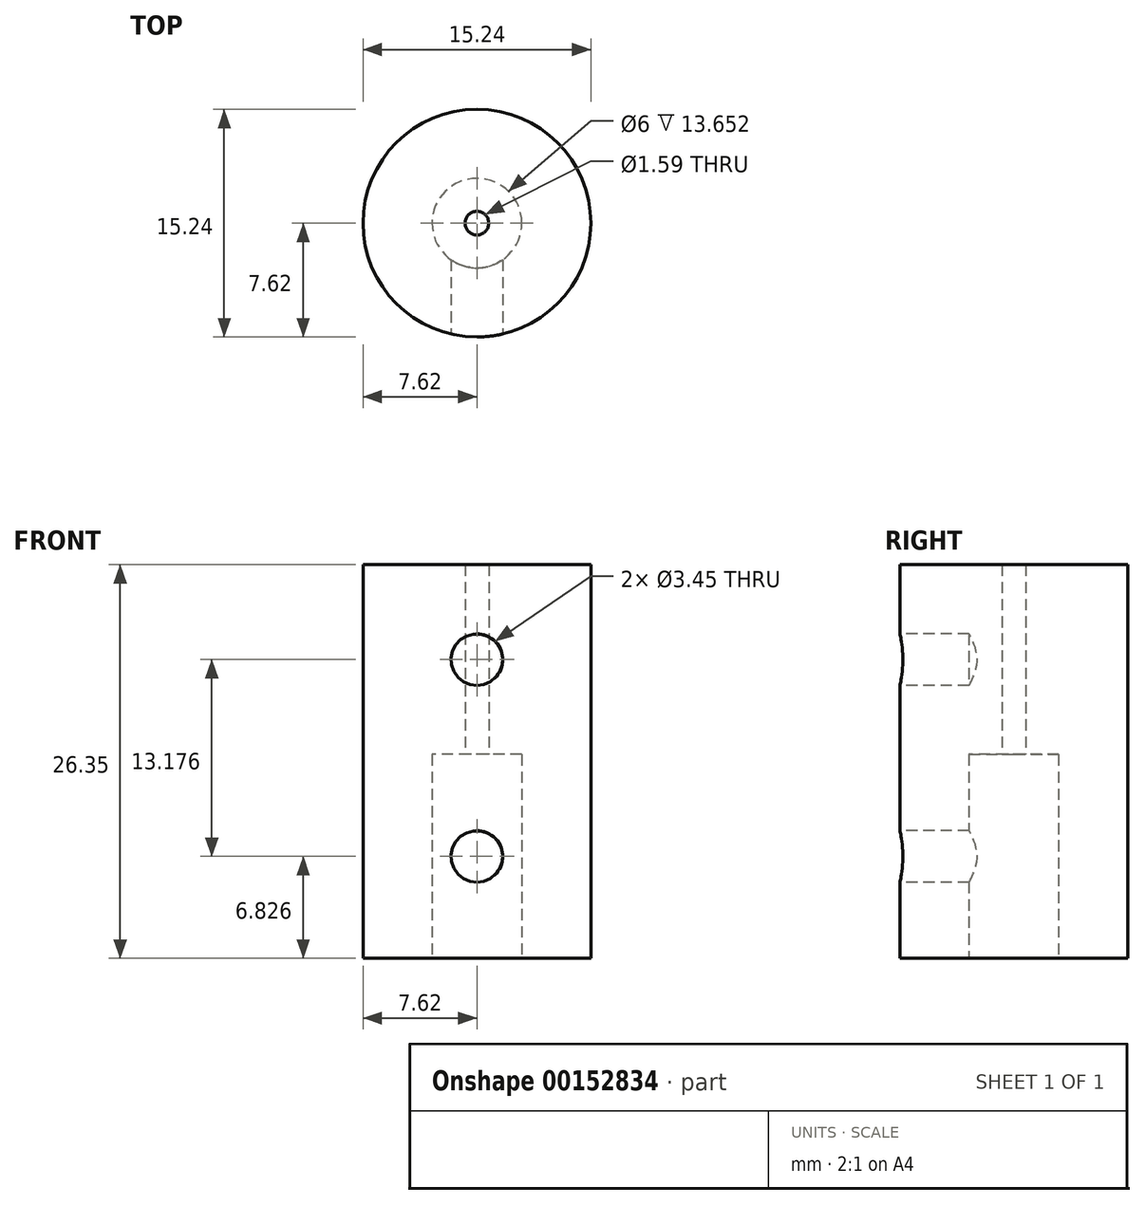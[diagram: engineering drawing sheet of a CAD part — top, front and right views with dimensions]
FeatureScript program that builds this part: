
annotation { "Feature Type Name" : "Feature", "Feature Type Description" : "" }
export const myFeature = defineFeature(function(context is Context, id is Id, definition is map)
    precondition{}
    {
        {
            var Q0;
            Q0=qCreatedBy(makeId("Top.planeOp"),FACE);
            var sketch = newSketch(context, id + "F0", { "sketchPlane" : qUnion([Q0])});
            skCircle(sketch, "E0", {"center": v(0, 0) * mm, "radius": 3 * mm});
            skCircle(sketch, "E1", {"center": v(0, 0) * mm, "radius": 12.7 * mm, "construction": true});
            skLineSegment(sketch, "E2.bottom", {"start": v(12.7, 12.7) * mm, "end": v(-12.7, 12.7) * mm});
            skLineSegment(sketch, "E2.top", {"start": v(12.7, -12.7) * mm, "end": v(-12.7, -12.7) * mm});
            skLineSegment(sketch, "E2.left", {"start": v(12.7, 12.7) * mm, "end": v(12.7, -12.7) * mm});
            skLineSegment(sketch, "E2.right", {"start": v(-12.7, 12.7) * mm, "end": v(-12.7, -12.7) * mm});
            skSolve(sketch);
        }
        {
            var Q0;
            Q0 = qSketchRegion(id + "F0", true);
            extrude(context, id + "F1", {"entities" : qUnion([Q0]), "depth" : 13.65 * mm});
        }
        {
            var Q0;
            Q0=makeQuery(id+"F1.opExtrude","CAP_FACE",FACE,{"disambiguationData":[OSD([sQuery(id+"F0.wireOp",EDGE,"E0"),sQuery(id+"F0.wireOp",EDGE,"E2.bottom"),sQuery(id+"F0.wireOp",EDGE,"E2.top"),sQuery(id+"F0.wireOp",EDGE,"E2.left"),sQuery(id+"F0.wireOp",EDGE,"E2.right")])],"isStart":false});
            var sketch = newSketch(context, id + "F2", { "sketchPlane" : qUnion([Q0])});
            skCircle(sketch, "E3", {"center": v(0, 0) * mm, "radius": 0.8 * mm});
            skLineSegment(sketch, "E4.bottom", {"start": v(12.7, 12.7) * mm, "end": v(-12.7, 12.7) * mm});
            skLineSegment(sketch, "E4.top", {"start": v(12.7, -12.7) * mm, "end": v(-12.7, -12.7) * mm});
            skLineSegment(sketch, "E4.left", {"start": v(12.7, 12.7) * mm, "end": v(12.7, -12.7) * mm});
            skLineSegment(sketch, "E4.right", {"start": v(-12.7, 12.7) * mm, "end": v(-12.7, -12.7) * mm});
            skSolve(sketch);
        }
        {
            var Q0;
            Q0 = qSketchRegion(id + "F2", true);
            extrude(context, id + "F3", {"entities" : qUnion([Q0]), "operationType" : NewBodyOperationType.ADD, "depth" : 12.7 * mm});
        }
        {
            var Q0;
            Q0=makeQuery(id+"F3.boolean.opBoolean","MERGE",FACE,{"derivedFrom":[makeQuery(id+"F1.opExtrude","SWEPT_FACE",FACE,{"disambiguationData":[OSD([sQuery(id+"F0.wireOp",EDGE,"E2.top")])]}),makeQuery(id+"F3.opExtrude","SWEPT_FACE",FACE,{"disambiguationData":[OSD([sQuery(id+"F2.wireOp",EDGE,"E4.top")])]})]});
            var sketch = newSketch(context, id + "F4", { "sketchPlane" : qUnion([Q0])});
            skLineSegment(sketch, "E5", {"start": v(0, 26.35) * mm, "end": v(0, 13.65) * mm, "construction": true});
            skLineSegment(sketch, "E6", {"start": v(0, 13.65) * mm, "end": v(0, 0) * mm, "construction": true});
            skCircle(sketch, "E7", {"center": v(0, 20) * mm, "radius": 1.73 * mm});
            skCircle(sketch, "E8", {"center": v(0, 6.83) * mm, "radius": 1.73 * mm});
            skSolve(sketch);
        }
        {
            var Q0;
            Q0 = qSketchRegion(id + "F4", true);
            var Q1;
            Q1=makeQuery(id+"F1.opExtrude","SWEPT_FACE",FACE,{"disambiguationData":[OSD([sQuery(id+"F0.wireOp",EDGE,"E0")])]});
            extrude(context, id + "F5", {"entities" : qUnion([Q0]), "operationType" : NewBodyOperationType.REMOVE, "endBound" : BoundingType.UP_TO_SURFACE, "oppositeDirection" : true, "endBoundEntityFace" : qUnion([Q1]), "depth" : 6.54 * mm});
        }
        {
            var Q0;
            Q0=makeQuery(id+"F1.opExtrude","CAP_FACE",FACE,{"disambiguationData":[OSD([sQuery(id+"F0.wireOp",EDGE,"E0"),sQuery(id+"F0.wireOp",EDGE,"E2.bottom"),sQuery(id+"F0.wireOp",EDGE,"E2.top"),sQuery(id+"F0.wireOp",EDGE,"E2.left"),sQuery(id+"F0.wireOp",EDGE,"E2.right")])],"isStart":true});
            var sketch = newSketch(context, id + "F6", { "sketchPlane" : qUnion([Q0])});
            skLineSegment(sketch, "E9.bottom", {"start": v(12.7, -12.7) * mm, "end": v(-12.7, -12.7) * mm});
            skLineSegment(sketch, "E9.top", {"start": v(12.7, 12.7) * mm, "end": v(-12.7, 12.7) * mm});
            skLineSegment(sketch, "E9.left", {"start": v(12.7, -12.7) * mm, "end": v(12.7, 12.7) * mm});
            skLineSegment(sketch, "E9.right", {"start": v(-12.7, -12.7) * mm, "end": v(-12.7, 12.7) * mm});
            skPoint(sketch, "E9.middle", {"position": v(0, 0) * mm});
            skCircle(sketch, "E10", {"center": v(0, 0) * mm, "radius": 7.62 * mm});
            skSolve(sketch);
        }
        {
            var Q0;
            Q0 = qSketchRegion(id + "F6", true);
            var Q1;
            Q1=makeQuery(id+"F3.opExtrude","CAP_FACE",FACE,{"disambiguationData":[OSD([sQuery(id+"F2.wireOp",EDGE,"E3"),sQuery(id+"F2.wireOp",EDGE,"E4.bottom"),sQuery(id+"F2.wireOp",EDGE,"E4.top"),sQuery(id+"F2.wireOp",EDGE,"E4.left"),sQuery(id+"F2.wireOp",EDGE,"E4.right")])],"isStart":false});
            extrude(context, id + "F7", {"entities" : qUnion([Q0]), "operationType" : NewBodyOperationType.REMOVE, "endBound" : BoundingType.UP_TO_SURFACE, "oppositeDirection" : true, "endBoundEntityFace" : qUnion([Q1]), "depth" : 25.4 * mm});
        }
    });
